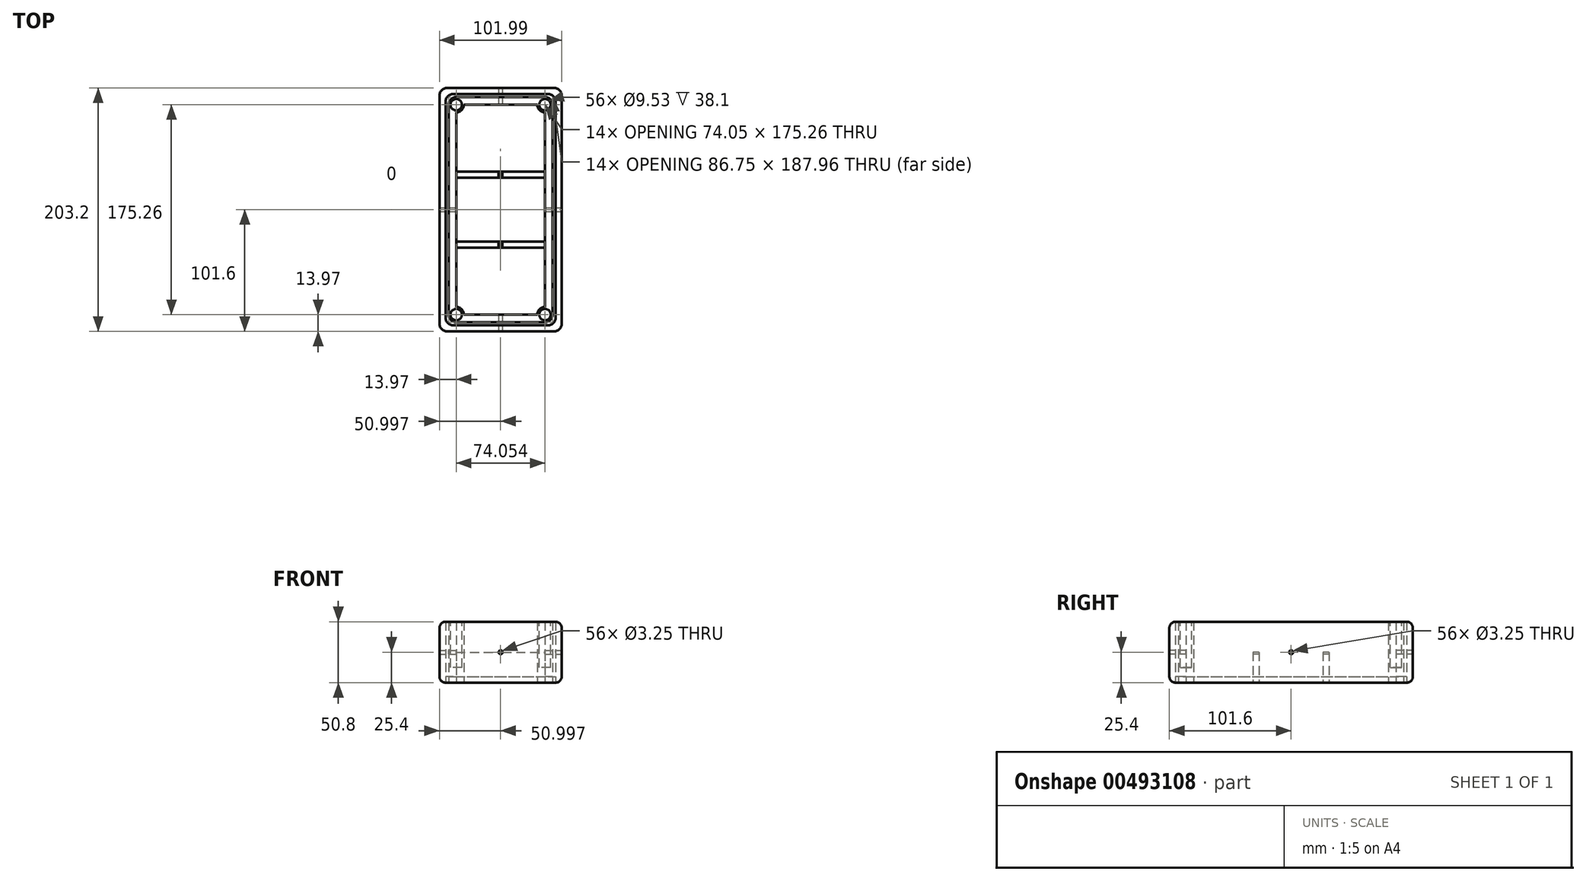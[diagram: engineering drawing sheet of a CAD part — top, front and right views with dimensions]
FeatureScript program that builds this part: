
annotation { "Feature Type Name" : "Feature", "Feature Type Description" : "" }
export const myFeature = defineFeature(function(context is Context, id is Id, definition is map)
    precondition{}
    {
        {
            var Q0;
            Q0=qCreatedBy(makeId("Top.planeOp"),FACE);
            var sketch = newSketch(context, id + "F0", { "sketchPlane" : qUnion([Q0])});
            skLineSegment(sketch, "E0.bottom", {"start": v(0, 0) * mm, "end": v(102, 0) * mm});
            skLineSegment(sketch, "E0.top", {"start": v(0, 203.2) * mm, "end": v(102, 203.2) * mm});
            skLineSegment(sketch, "E0.left", {"start": v(0, 0) * mm, "end": v(0, 203.2) * mm});
            skLineSegment(sketch, "E0.right", {"start": v(102, 0) * mm, "end": v(102, 203.2) * mm});
            skLineSegment(sketch, "E1.bottom", {"start": v(5.08, 5.08) * mm, "end": v(96.91, 5.08) * mm});
            skLineSegment(sketch, "E1.top", {"start": v(5.08, 198.12) * mm, "end": v(96.91, 198.12) * mm});
            skLineSegment(sketch, "E1.left", {"start": v(5.08, 5.08) * mm, "end": v(5.08, 198.12) * mm});
            skLineSegment(sketch, "E1.right", {"start": v(96.91, 5.08) * mm, "end": v(96.91, 198.12) * mm});
            skLineSegment(sketch, "E2.bottom", {"start": v(7.62, 7.62) * mm, "end": v(94.37, 7.62) * mm});
            skLineSegment(sketch, "E2.top", {"start": v(7.62, 195.58) * mm, "end": v(94.37, 195.58) * mm});
            skLineSegment(sketch, "E2.left", {"start": v(7.62, 7.62) * mm, "end": v(7.62, 195.58) * mm});
            skLineSegment(sketch, "E2.right", {"start": v(94.37, 7.62) * mm, "end": v(94.37, 195.58) * mm});
            skLineSegment(sketch, "E3.bottom", {"start": v(13.97, 13.97) * mm, "end": v(88.02, 13.97) * mm, "construction": true});
            skLineSegment(sketch, "E3.top", {"start": v(13.97, 189.23) * mm, "end": v(88.02, 189.23) * mm, "construction": true});
            skLineSegment(sketch, "E3.left", {"start": v(13.97, 13.97) * mm, "end": v(13.97, 189.23) * mm, "construction": true});
            skLineSegment(sketch, "E3.right", {"start": v(88.02, 13.97) * mm, "end": v(88.02, 189.23) * mm, "construction": true});
            skCircle(sketch, "E4", {"center": v(13.97, 189.23) * mm, "radius": 6.35 * mm, "construction": true});
            skCircle(sketch, "E5", {"center": v(88.02, 189.23) * mm, "radius": 6.35 * mm, "construction": true});
            skCircle(sketch, "E6", {"center": v(88.02, 13.97) * mm, "radius": 6.35 * mm, "construction": true});
            skCircle(sketch, "E7", {"center": v(13.97, 13.97) * mm, "radius": 6.35 * mm, "construction": true});
            skArc(sketch, "E8", {"start": v(13.97, 182.88) * mm, "mid": v(18.46, 184.74) * mm, "end": v(20.32, 189.23) * mm});
            skArc(sketch, "E9", {"start": v(81.67, 189.23) * mm, "mid": v(83.53, 184.74) * mm, "end": v(88.02, 182.88) * mm});
            skArc(sketch, "E10", {"start": v(88.02, 20.32) * mm, "mid": v(83.53, 18.46) * mm, "end": v(81.67, 13.97) * mm});
            skArc(sketch, "E11", {"start": v(20.32, 13.97) * mm, "mid": v(18.46, 18.46) * mm, "end": v(13.97, 20.32) * mm});
            skLineSegment(sketch, "E12", {"start": v(20.32, 189.23) * mm, "end": v(81.67, 189.23) * mm});
            skLineSegment(sketch, "E13", {"start": v(88.02, 182.88) * mm, "end": v(88.02, 20.32) * mm});
            skLineSegment(sketch, "E14", {"start": v(81.67, 13.97) * mm, "end": v(20.32, 13.97) * mm});
            skLineSegment(sketch, "E15", {"start": v(13.97, 20.32) * mm, "end": v(13.97, 182.88) * mm});
            skLineSegment(sketch, "E16.bottom", {"start": v(13.97, 128.27) * mm, "end": v(88.02, 128.27) * mm});
            skLineSegment(sketch, "E16.top", {"start": v(13.97, 133.35) * mm, "end": v(88.02, 133.35) * mm});
            skLineSegment(sketch, "E16.left", {"start": v(13.97, 128.27) * mm, "end": v(13.97, 133.35) * mm});
            skLineSegment(sketch, "E16.right", {"start": v(88.02, 128.27) * mm, "end": v(88.02, 133.35) * mm});
            skLineSegment(sketch, "E17.bottom", {"start": v(13.97, 74.93) * mm, "end": v(88.02, 74.93) * mm});
            skLineSegment(sketch, "E17.top", {"start": v(13.97, 69.85) * mm, "end": v(88.02, 69.85) * mm});
            skLineSegment(sketch, "E17.left", {"start": v(13.97, 69.85) * mm, "end": v(13.97, 74.93) * mm});
            skLineSegment(sketch, "E17.right", {"start": v(88.02, 69.85) * mm, "end": v(88.02, 74.93) * mm});
            skLineSegment(sketch, "E18", {"start": v(13.97, 130.81) * mm, "end": v(88.02, 130.81) * mm, "construction": true});
            skLineSegment(sketch, "E19", {"start": v(13.97, 72.4) * mm, "end": v(88.02, 72.4) * mm, "construction": true});
            skSolve(sketch);
        }
        {
            var Q0;
            Q0=makeQuery(id+"F0.imprint","IMPRINT",FACE,{"disambiguationData":[TD([[makeQuery(id+"F0.imprint","IMPRINT",EDGE,{"derivedFrom":sQuery(id+"F0.wireOp",EDGE,"E0.bottom")}),1.0]])]});
            var Q1;
            Q1=makeQuery(id+"F0.imprint","IMPRINT",FACE,{"disambiguationData":[TD([[makeQuery(id+"F0.imprint","IMPRINT",EDGE,{"derivedFrom":sQuery(id+"F0.wireOp",EDGE,"E2.bottom")}),1.0]])]});
            extrude(context, id + "F1", {"entities" : qUnion([Q0, Q1]), "depth" : 50.8 * mm});
        }
        {
            var Q0;
            Q0=makeQuery(id+"F0.imprint","IMPRINT",FACE,{"disambiguationData":[TD([[makeQuery(id+"F0.imprint","IMPRINT",EDGE,{"derivedFrom":sQuery(id+"F0.wireOp",EDGE,"E1.bottom")}),1.0]])]});
            extrude(context, id + "F2", {"entities" : qUnion([Q0]), "depth" : 5.08 * mm});
        }
        {
            var Q0;
            Q0=makeQuery(id+"F0.imprint","IMPRINT",FACE,{"disambiguationData":[TD([[makeQuery(id+"F0.imprint","IMPRINT",EDGE,{"derivedFrom":sQuery(id+"F0.wireOp",EDGE,"E16.bottom")}),1.0]])]});
            var Q1;
            Q1=makeQuery(id+"F0.imprint","IMPRINT",FACE,{"disambiguationData":[TD([[makeQuery(id+"F0.imprint","IMPRINT",EDGE,{"derivedFrom":sQuery(id+"F0.wireOp",EDGE,"E17.bottom")}),-1.0]])]});
            extrude(context, id + "F3", {"entities" : qUnion([Q0, Q1]), "depth" : 25.4 * mm});
        }
        {
            var Q0;
            Q0=makeQuery(id+"F1.opExtrude","SWEPT_EDGE",EDGE,{"disambiguationData":[OSD([sQuery(id+"F0.wireOp",EDGE,"E0.bottom"),sQuery(id+"F0.wireOp",EDGE,"E0.right")])]});
            var Q1;
            Q1=makeQuery(id+"F1.opExtrude","SWEPT_EDGE",EDGE,{"disambiguationData":[OSD([sQuery(id+"F0.wireOp",EDGE,"E0.bottom"),sQuery(id+"F0.wireOp",EDGE,"E0.left")])]});
            var Q2;
            Q2=makeQuery(id+"F1.opExtrude","SWEPT_EDGE",EDGE,{"disambiguationData":[OSD([sQuery(id+"F0.wireOp",EDGE,"E1.bottom"),sQuery(id+"F0.wireOp",EDGE,"E1.right")])]});
            var Q3;
            Q3=makeQuery(id+"F1.opExtrude","SWEPT_EDGE",EDGE,{"disambiguationData":[OSD([sQuery(id+"F0.wireOp",EDGE,"E2.bottom"),sQuery(id+"F0.wireOp",EDGE,"E2.right")])]});
            var Q4;
            Q4=makeQuery(id+"F1.opExtrude","SWEPT_EDGE",EDGE,{"disambiguationData":[OSD([sQuery(id+"F0.wireOp",EDGE,"E2.bottom"),sQuery(id+"F0.wireOp",EDGE,"E2.left")])]});
            var Q5;
            Q5=makeQuery(id+"F1.opExtrude","SWEPT_EDGE",EDGE,{"disambiguationData":[OSD([sQuery(id+"F0.wireOp",EDGE,"E1.bottom"),sQuery(id+"F0.wireOp",EDGE,"E1.left")])]});
            var Q6;
            Q6=makeQuery(id+"F1.opExtrude","SWEPT_EDGE",EDGE,{"disambiguationData":[OSD([sQuery(id+"F0.wireOp",EDGE,"E0.top"),sQuery(id+"F0.wireOp",EDGE,"E0.right")])]});
            var Q7;
            Q7=makeQuery(id+"F1.opExtrude","SWEPT_EDGE",EDGE,{"disambiguationData":[OSD([sQuery(id+"F0.wireOp",EDGE,"E0.top"),sQuery(id+"F0.wireOp",EDGE,"E0.left")])]});
            var Q8;
            Q8=makeQuery(id+"F1.opExtrude","SWEPT_EDGE",EDGE,{"disambiguationData":[OSD([sQuery(id+"F0.wireOp",EDGE,"E2.top"),sQuery(id+"F0.wireOp",EDGE,"E2.left")])]});
            var Q9;
            Q9=makeQuery(id+"F1.opExtrude","SWEPT_EDGE",EDGE,{"disambiguationData":[OSD([sQuery(id+"F0.wireOp",EDGE,"E2.top"),sQuery(id+"F0.wireOp",EDGE,"E2.right")])]});
            var Q10;
            Q10=makeQuery(id+"F1.opExtrude","SWEPT_EDGE",EDGE,{"disambiguationData":[OSD([sQuery(id+"F0.wireOp",EDGE,"E1.top"),sQuery(id+"F0.wireOp",EDGE,"E1.right")])]});
            var Q11;
            Q11=makeQuery(id+"F1.opExtrude","SWEPT_EDGE",EDGE,{"disambiguationData":[OSD([sQuery(id+"F0.wireOp",EDGE,"E1.top"),sQuery(id+"F0.wireOp",EDGE,"E1.left")])]});
            fillet(context, id + "F4", {"entities" : qUnion([Q0, Q1, Q2, Q3, Q4, Q5, Q6, Q7, Q8, Q9, Q10, Q11]), "radius" : 6.35 * mm, "tangentPropagation" : true, "allowEdgeOverflow" : false});
        }
        {
            var Q0;
            Q0=makeQuery(id+"F2.opExtrude","SWEPT_EDGE",EDGE,{"disambiguationData":[OSD([sQuery(id+"F0.wireOp",EDGE,"E2.bottom"),sQuery(id+"F0.wireOp",EDGE,"E2.left")])]});
            var Q1;
            Q1=makeQuery(id+"F2.opExtrude","SWEPT_EDGE",EDGE,{"disambiguationData":[OSD([sQuery(id+"F0.wireOp",EDGE,"E1.bottom"),sQuery(id+"F0.wireOp",EDGE,"E1.left")])]});
            var Q2;
            Q2=makeQuery(id+"F2.opExtrude","SWEPT_EDGE",EDGE,{"disambiguationData":[OSD([sQuery(id+"F0.wireOp",EDGE,"E2.bottom"),sQuery(id+"F0.wireOp",EDGE,"E2.right")])]});
            var Q3;
            Q3=makeQuery(id+"F2.opExtrude","SWEPT_EDGE",EDGE,{"disambiguationData":[OSD([sQuery(id+"F0.wireOp",EDGE,"E1.bottom"),sQuery(id+"F0.wireOp",EDGE,"E1.right")])]});
            var Q4;
            Q4=makeQuery(id+"F2.opExtrude","SWEPT_EDGE",EDGE,{"disambiguationData":[OSD([sQuery(id+"F0.wireOp",EDGE,"E2.top"),sQuery(id+"F0.wireOp",EDGE,"E2.left")])]});
            var Q5;
            Q5=makeQuery(id+"F2.opExtrude","SWEPT_EDGE",EDGE,{"disambiguationData":[OSD([sQuery(id+"F0.wireOp",EDGE,"E1.top"),sQuery(id+"F0.wireOp",EDGE,"E1.right")])]});
            var Q6;
            Q6=makeQuery(id+"F2.opExtrude","SWEPT_EDGE",EDGE,{"disambiguationData":[OSD([sQuery(id+"F0.wireOp",EDGE,"E2.top"),sQuery(id+"F0.wireOp",EDGE,"E2.right")])]});
            var Q7;
            Q7=makeQuery(id+"F2.opExtrude","SWEPT_EDGE",EDGE,{"disambiguationData":[OSD([sQuery(id+"F0.wireOp",EDGE,"E1.top"),sQuery(id+"F0.wireOp",EDGE,"E1.left")])]});
            fillet(context, id + "F5", {"entities" : qUnion([Q0, Q1, Q2, Q3, Q4, Q5, Q6, Q7]), "radius" : 6.35 * mm, "tangentPropagation" : true, "allowEdgeOverflow" : false});
        }
        {
            var Q0;
            Q0=makeQuery(id+"F1.opExtrude","SWEPT_FACE",FACE,{"disambiguationData":[OSD([sQuery(id+"F0.wireOp",EDGE,"E0.right")])]});
            var sketch = newSketch(context, id + "F6", { "sketchPlane" : qUnion([Q0])});
            skCircle(sketch, "E20", {"center": v(101.6, 25.4) * mm, "radius": 1.63 * mm});
            skLineSegment(sketch, "E21", {"start": v(6.35, 25.4) * mm, "end": v(196.85, 25.4) * mm, "construction": true});
            skLineSegment(sketch, "E22", {"start": v(101.6, 0) * mm, "end": v(101.6, 50.8) * mm, "construction": true});
            skSolve(sketch);
        }
        {
            var Q0;
            Q0=makeQuery(id+"F1.opExtrude","SWEPT_FACE",FACE,{"disambiguationData":[OSD([sQuery(id+"F0.wireOp",EDGE,"E0.bottom")])]});
            var sketch = newSketch(context, id + "F7", { "sketchPlane" : qUnion([Q0])});
            skLineSegment(sketch, "E23", {"start": v(6.35, 25.4) * mm, "end": v(95.64, 25.4) * mm, "construction": true});
            skLineSegment(sketch, "E24", {"start": v(51, 0) * mm, "end": v(51, 50.8) * mm, "construction": true});
            skCircle(sketch, "E25", {"center": v(51, 25.4) * mm, "radius": 1.63 * mm});
            skSolve(sketch);
        }
        {
            var Q0;
            Q0=makeQuery(id+"F6.imprint","IMPRINT",FACE,{"disambiguationData":[TD([[makeQuery(id+"F6.imprint","IMPRINT",EDGE,{"derivedFrom":sQuery(id+"F6.wireOp",EDGE,"E20")}),1.0]])]});
            extrude(context, id + "F8", {"entities" : qUnion([Q0]), "operationType" : NewBodyOperationType.REMOVE, "oppositeDirection" : true, "depth" : 127 * mm});
        }
        {
            var Q0;
            Q0=makeQuery(id+"F7.imprint","IMPRINT",FACE,{"disambiguationData":[TD([[makeQuery(id+"F7.imprint","IMPRINT",EDGE,{"derivedFrom":sQuery(id+"F7.wireOp",EDGE,"E25")}),1.0]])]});
            extrude(context, id + "F9", {"entities" : qUnion([Q0]), "operationType" : NewBodyOperationType.REMOVE, "oppositeDirection" : true, "depth" : 254 * mm});
        }
        {
            var Q0;
            Q0=makeQuery(id+"F1.opExtrude","CAP_FACE",FACE,{"disambiguationData":[OSD([sQuery(id+"F0.wireOp",EDGE,"E2.bottom"),sQuery(id+"F0.wireOp",EDGE,"E2.top"),sQuery(id+"F0.wireOp",EDGE,"E2.left"),sQuery(id+"F0.wireOp",EDGE,"E2.right"),sQuery(id+"F0.wireOp",EDGE,"E8"),sQuery(id+"F0.wireOp",EDGE,"E9"),sQuery(id+"F0.wireOp",EDGE,"E10"),sQuery(id+"F0.wireOp",EDGE,"E11"),sQuery(id+"F0.wireOp",EDGE,"E12"),sQuery(id+"F0.wireOp",EDGE,"E13"),sQuery(id+"F0.wireOp",EDGE,"E14"),sQuery(id+"F0.wireOp",EDGE,"E15"),sQuery(id+"F0.wireOp",EDGE,"E16.left"),sQuery(id+"F0.wireOp",EDGE,"E16.right"),sQuery(id+"F0.wireOp",EDGE,"E17.left"),sQuery(id+"F0.wireOp",EDGE,"E17.right")])],"isStart":false});
            var sketch = newSketch(context, id + "F10", { "sketchPlane" : qUnion([Q0])});
            skCircle(sketch, "E26", {"center": v(13.97, 189.23) * mm, "radius": 4.76 * mm});
            skCircle(sketch, "E27", {"center": v(88.02, 189.23) * mm, "radius": 4.76 * mm});
            skCircle(sketch, "E28", {"center": v(88.02, 13.97) * mm, "radius": 4.76 * mm});
            skCircle(sketch, "E29", {"center": v(13.97, 13.97) * mm, "radius": 4.76 * mm});
            skSolve(sketch);
        }
        {
            var Q0;
            Q0=makeQuery(id+"F10.imprint","IMPRINT",FACE,{"disambiguationData":[TD([[makeQuery(id+"F10.imprint","IMPRINT",EDGE,{"derivedFrom":sQuery(id+"F10.wireOp",EDGE,"E28")}),1.0]])]});
            var Q1;
            Q1=makeQuery(id+"F10.imprint","IMPRINT",FACE,{"disambiguationData":[TD([[makeQuery(id+"F10.imprint","IMPRINT",EDGE,{"derivedFrom":sQuery(id+"F10.wireOp",EDGE,"E29")}),1.0]])]});
            var Q2;
            Q2=makeQuery(id+"F10.imprint","IMPRINT",FACE,{"disambiguationData":[TD([[makeQuery(id+"F10.imprint","IMPRINT",EDGE,{"derivedFrom":sQuery(id+"F10.wireOp",EDGE,"E26")}),1.0]])]});
            var Q3;
            Q3=makeQuery(id+"F10.imprint","IMPRINT",FACE,{"disambiguationData":[TD([[makeQuery(id+"F10.imprint","IMPRINT",EDGE,{"derivedFrom":sQuery(id+"F10.wireOp",EDGE,"E27")}),1.0]])]});
            extrude(context, id + "F11", {"entities" : qUnion([Q0, Q1, Q2, Q3]), "operationType" : NewBodyOperationType.REMOVE, "oppositeDirection" : true, "depth" : 38.1 * mm});
        }
        {
            var Q0;
            Q0=makeQuery(id+"F1.opExtrude","CAP_EDGE",EDGE,{"disambiguationData":[OSD([sQuery(id+"F0.wireOp",EDGE,"E0.right")])],"isStart":true});
            var Q1;
            Q1=makeQuery(id+"F1.opExtrude","CAP_EDGE",EDGE,{"disambiguationData":[OSD([sQuery(id+"F0.wireOp",EDGE,"E0.right")])],"isStart":false});
            fillet(context, id + "F12", {"entities" : qUnion([Q0, Q1]), "radius" : 5.08 * mm, "tangentPropagation" : true, "allowEdgeOverflow" : false});
        }
    });
